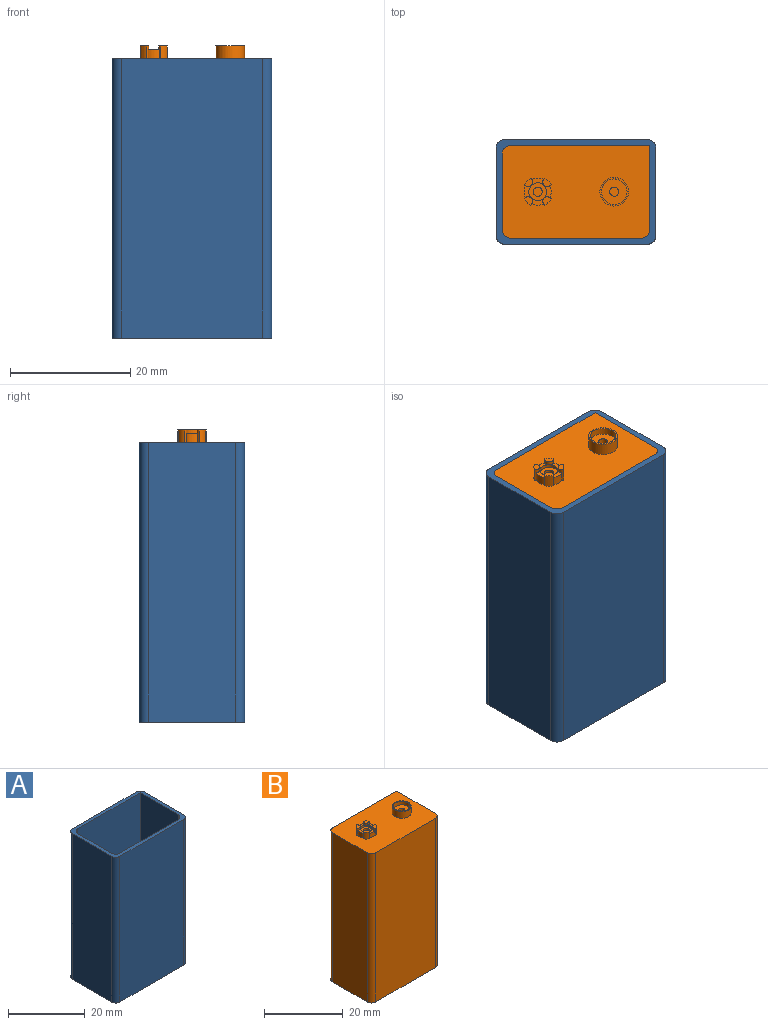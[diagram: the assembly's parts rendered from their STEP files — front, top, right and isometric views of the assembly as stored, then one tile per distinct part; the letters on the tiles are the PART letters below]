
ASSEMBLY  parts=2 mates=1
PART A: 17 faces, bbox 26.5x17.5x46.4 mm
  f0: plane 46.4x23.5mm, normal (0,1,0), area 1090.4mm2, adj f1,f14,f15,f16
  f1: cylinder r=1.5mm len=46.4mm, axis (0,0,1), area 109.3mm2, adj f0,f2,f15,f16
  f2: plane 46.4x14.5mm, normal (-1,0,0), area 672.8mm2, adj f1,f3,f15,f16
  f3: cylinder r=1.5mm len=46.4mm, axis (0,0,1), area 109.3mm2, adj f2,f4,f15,f16
  f4: plane 46.4x23.5mm, normal (0,-1,0), area 1090.4mm2, adj f3,f5,f15,f16
  f5: cylinder r=1.5mm len=46.4mm, axis (0,0,1), area 109.3mm2, adj f4,f6,f15,f16
  f6: plane 46.4x14.5mm, normal (1,0,0), area 672.8mm2, adj f5,f14,f15,f16
  f7: cylinder r=1.5mm len=46.4mm, axis (0,0,1), area 109.3mm2, adj f8,f13,f15,f16
  f8: plane 46.4x21.5mm, normal (0,1,0), area 997.6mm2, adj f7,f9,f15,f16
  f9: cylinder r=1.5mm len=46.4mm, axis (0,0,1), area 109.3mm2, adj f8,f10,f15,f16
  f10: plane 46.4x12.5mm, normal (1,0,0), area 580mm2, adj f9,f11,f15,f16
  f11: cylinder r=1.5mm len=46.4mm, axis (0,0,1), area 109.3mm2, adj f10,f12,f15,f16
  f12: plane 46.4x23mm, normal (0,-1,0), area 1067.2mm2, adj f11,f13,f15,f16
  f13: plane 46.4x14mm, normal (-1,0,0), area 649.6mm2, adj f7,f12,f15,f16
  f14: cylinder r=1.5mm len=46.4mm, axis (0,0,1), area 109.3mm2, adj f0,f6,f15,f16
  f15: plane 26.5x17.5mm, normal (0,0,-1), area 83.5mm2, adj f0,f1,f2,f3,f4,f5,f6,f7
  f16: plane 26.5x17.5mm, normal (0,0,1), area 83.5mm2, adj f0,f1,f2,f3,f4,f5,f6,f7
PART B: 39 faces, bbox 24.5x15.5x48.5 mm
  f0: cylinder r=0.75mm len=2.1mm, axis (0,0,-1), area 2.4mm2, adj f1,f19,f20,f28,f29,f34,f35
  f1: plane 24.5x15.5mm, normal (0,0,1), area 343.2mm2, adj f0,f2,f3,f4,f5,f6,f7,f8
  f2: cylinder r=0.75mm len=2.1mm, axis (0,0,-1), area 2.4mm2, adj f1,f21,f22,f30,f31,f32,f33
  f3: cylinder r=0.75mm len=2.1mm, axis (0,0,-1), area 2.4mm2, adj f1,f25,f26,f30,f31,f34,f35
  f4: cylinder r=0.75mm len=2.1mm, axis (0,0,-1), area 2.4mm2, adj f1,f23,f24,f28,f29,f32,f33
  f5: plane 46.4x21.5mm, normal (0,-1,0), area 997.6mm2, adj f1,f6,f11,f12
  f6: cylinder r=1.5mm len=46.4mm, axis (0,0,1), area 109.3mm2, adj f1,f5,f7,f12
  f7: plane 46.4x14mm, normal (1,0,0), area 649.6mm2, adj f1,f6,f8,f12
  f8: plane 46.4x23mm, normal (0,1,0), area 1067.2mm2, adj f1,f7,f9,f12
  f9: cylinder r=1.5mm len=46.4mm, axis (0,0,1), area 109.3mm2, adj f1,f8,f10,f12
  f10: plane 46.4x12.5mm, normal (-1,0,0), area 580mm2, adj f1,f9,f11,f12
  f11: cylinder r=1.5mm len=46.4mm, axis (0,0,1), area 109.3mm2, adj f1,f5,f10,f12
  f12: plane 24.5x15.5mm, normal (0,0,-1), area 378.3mm2, adj f5,f6,f7,f8,f9,f10,f11
  f13: cylinder r=2.12mm len=4.25mm, axis (0,0,-1), area 14.7mm2, adj f15,f17
  f14: cylinder r=2.38mm len=4.75mm, axis (0,0,-1), area 31.3mm2, adj f1,f15
  f15: plane 4.75x4.75mm, normal (0,0,1), area 3.5mm2, adj f13,f14
  f16: cylinder r=0.75mm len=1.5mm, axis (0,0,-1), area 4.7mm2, adj f17,f18
  f17: plane 4.25x4.25mm, normal (0,0,1), area 12.4mm2, adj f13,f16
  f18: plane 1.5x1.5mm, normal (0,0,1), area 1.8mm2, adj f16
  f19: cylinder r=2.5mm len=2.1mm, axis (0,0,-1), area 3.1mm2, adj f0,f1,f20
  f20: plane 1.37x1.37mm, normal (0,0,1), area 1.2mm2, adj f0,f19
  f21: cylinder r=2.5mm len=2.1mm, axis (0,0,-1), area 3.1mm2, adj f1,f2,f22
  f22: plane 1.37x1.37mm, normal (0,0,1), area 1.2mm2, adj f2,f21
  f23: cylinder r=2.5mm len=2.1mm, axis (0,0,-1), area 3.1mm2, adj f1,f4,f24
  f24: plane 1.37x1.37mm, normal (0,0,1), area 1.2mm2, adj f4,f23
  f25: cylinder r=2.5mm len=2.1mm, axis (0,0,-1), area 3.1mm2, adj f1,f3,f26
  f26: plane 1.37x1.37mm, normal (0,0,1), area 1.2mm2, adj f3,f25
  f27: cylinder r=1.5mm len=3mm, axis (0,0,-1), area 4.7mm2, adj f29,f31,f33,f35,f37
  f28: cylinder r=2.25mm len=1.96mm, axis (0,0,-1), area 3mm2, adj f0,f1,f4,f29
  f29: plane 2.12x1.19mm, normal (0,0,1), area 1.4mm2, adj f0,f4,f27,f28
  f30: cylinder r=2.25mm len=1.96mm, axis (0,0,-1), area 3mm2, adj f1,f2,f3,f31
  f31: plane 2.12x1.19mm, normal (0,0,1), area 1.4mm2, adj f2,f3,f27,f30
  f32: cylinder r=2.25mm len=1.96mm, axis (0,0,-1), area 3mm2, adj f1,f2,f4,f33
  f33: plane 2.12x1.19mm, normal (0,0,1), area 1.4mm2, adj f2,f4,f27,f32
  f34: cylinder r=2.25mm len=1.96mm, axis (0,0,-1), area 3mm2, adj f0,f1,f3,f35
  f35: plane 2.12x1.19mm, normal (0,0,1), area 1.4mm2, adj f0,f3,f27,f34
  f36: cylinder r=0.75mm len=1.5mm, axis (0,0,-1), area 4.7mm2, adj f37,f38
  f37: plane 3x3mm, normal (0,0,1), area 5.3mm2, adj f27,f36
  f38: plane 1.5x1.5mm, normal (0,0,1), area 1.8mm2, adj f36
PLACE A t=(26.5,5.19,8.04)mm
PLACE B t=(26.5,5.19,8.04)mm
MATE fastened B.f1 <-> A.f16  axis (0,0,1) through (14.25,-1.06,8.04)mm
